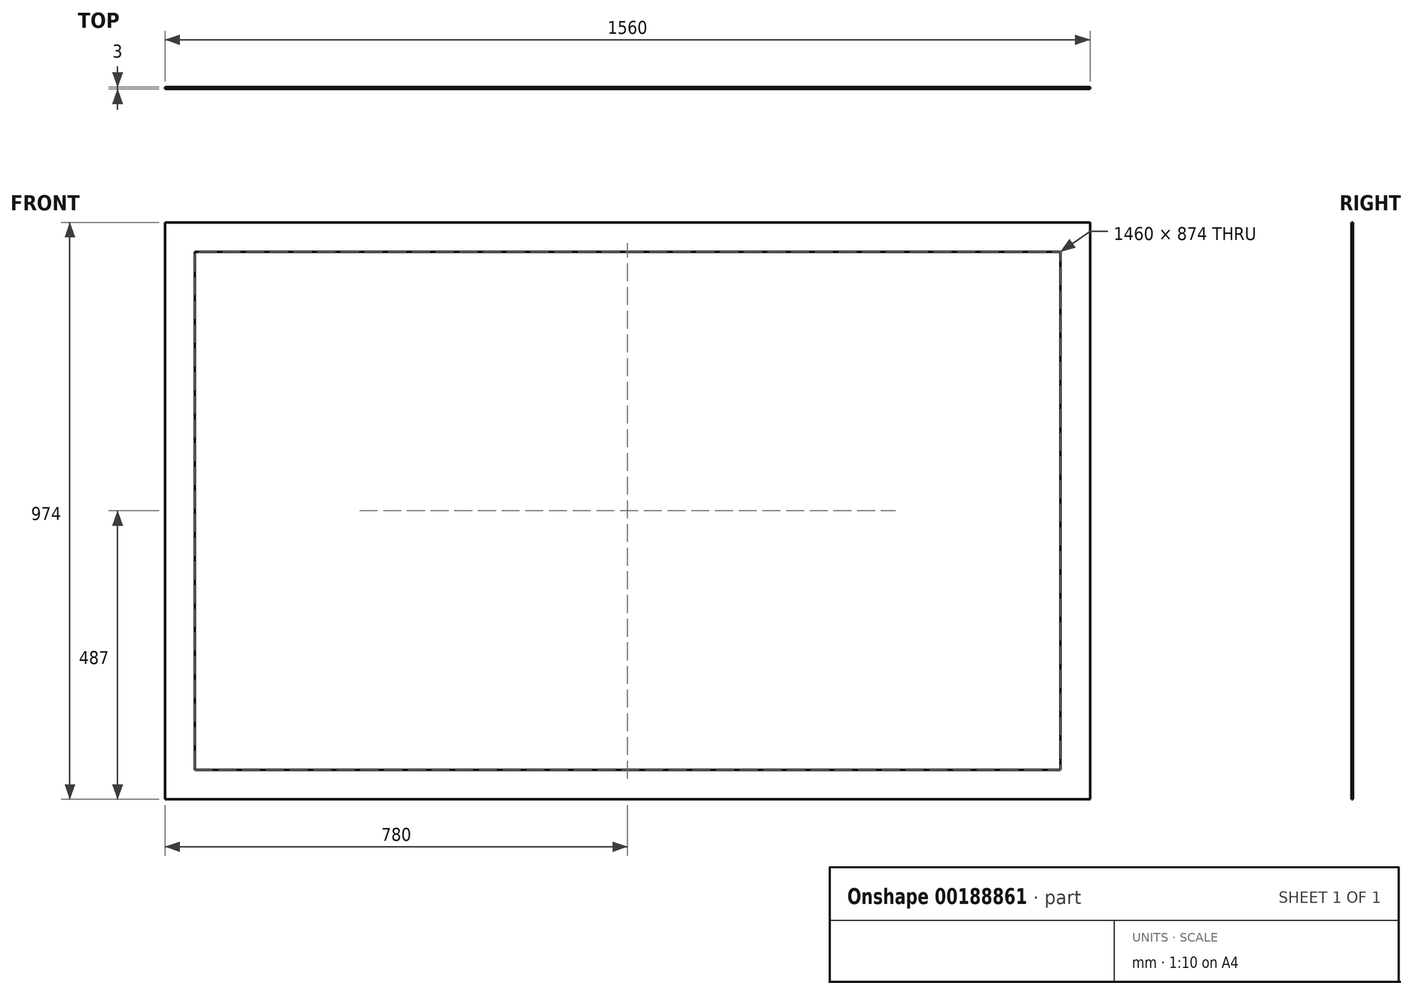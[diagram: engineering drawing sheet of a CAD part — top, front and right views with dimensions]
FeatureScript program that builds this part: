
annotation { "Feature Type Name" : "Feature", "Feature Type Description" : "" }
export const myFeature = defineFeature(function(context is Context, id is Id, definition is map)
    precondition{}
    {
        {
            var Q0;
            Q0=qCreatedBy(makeId("Front.planeOp"),FACE);
            var sketch = newSketch(context, id + "F0", { "sketchPlane" : qUnion([Q0])});
            skLineSegment(sketch, "E0.bottom", {"start": v(0, 0) * mm, "end": v(1560, 0) * mm});
            skLineSegment(sketch, "E0.top", {"start": v(0, -974) * mm, "end": v(1560, -974) * mm});
            skLineSegment(sketch, "E0.left", {"start": v(0, 0) * mm, "end": v(0, -974) * mm});
            skLineSegment(sketch, "E0.right", {"start": v(1560, 0) * mm, "end": v(1560, -974) * mm});
            skLineSegment(sketch, "E1.bottom", {"start": v(50, -50) * mm, "end": v(1510, -50) * mm});
            skLineSegment(sketch, "E1.top", {"start": v(50, -924) * mm, "end": v(1510, -924) * mm});
            skLineSegment(sketch, "E1.left", {"start": v(50, -50) * mm, "end": v(50, -924) * mm});
            skLineSegment(sketch, "E1.right", {"start": v(1510, -50) * mm, "end": v(1510, -924) * mm});
            skSolve(sketch);
        }
        {
            var Q0;
            Q0=makeQuery(id+"F0.imprint","IMPRINT",FACE,{"disambiguationData":[TD([[makeQuery(id+"F0.imprint","IMPRINT",EDGE,{"derivedFrom":sQuery(id+"F0.wireOp",EDGE,"E0.bottom")}),-1.0]])]});
            extrude(context, id + "F1", {"entities" : qUnion([Q0]), "depth" : 3 * mm});
        }
    });
